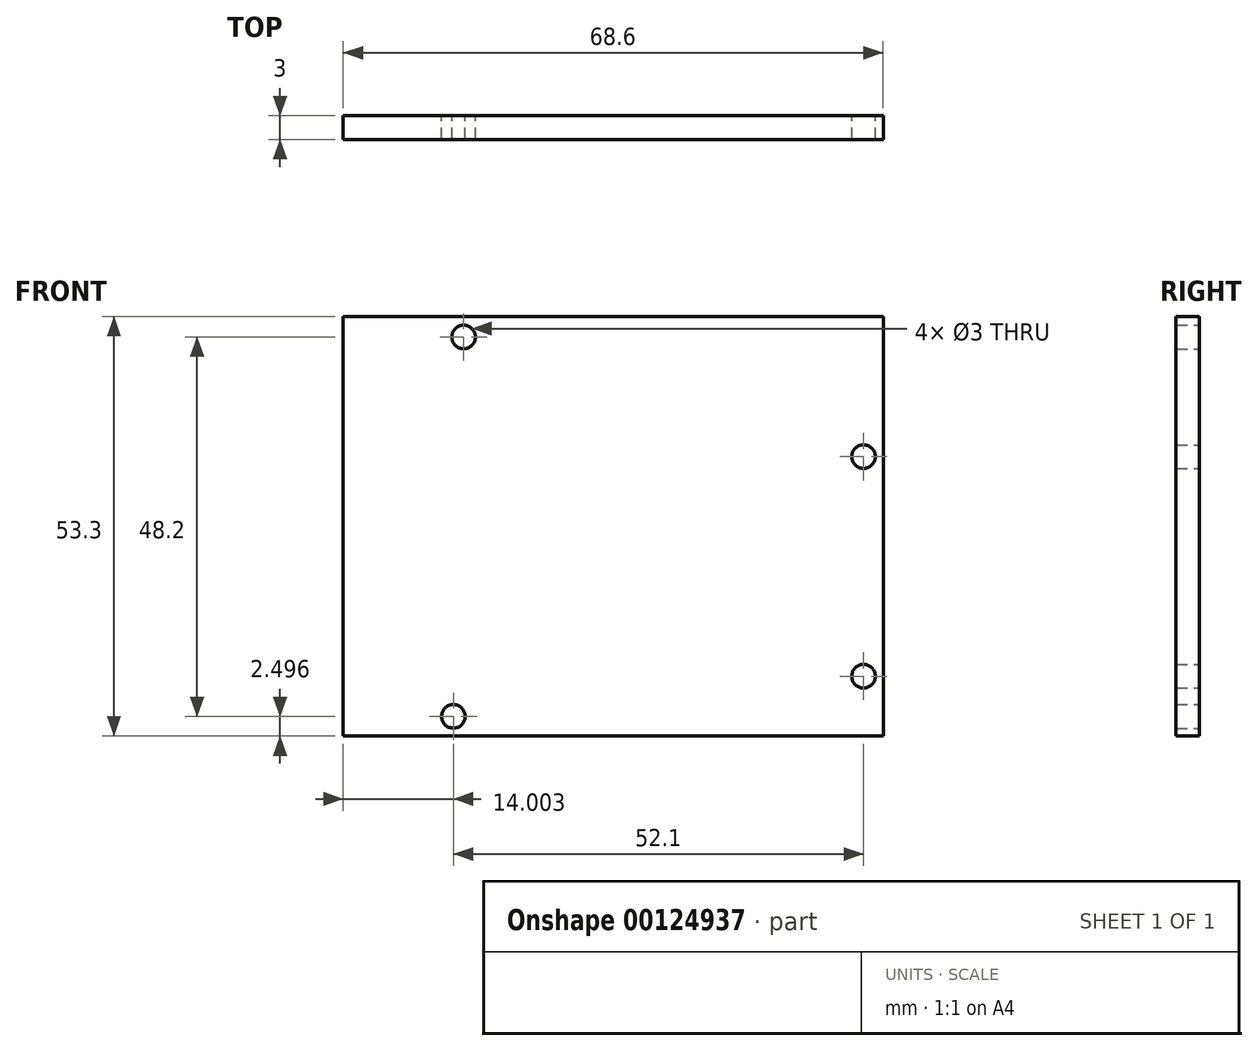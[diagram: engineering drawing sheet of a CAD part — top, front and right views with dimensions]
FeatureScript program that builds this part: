
annotation { "Feature Type Name" : "Feature", "Feature Type Description" : "" }
export const myFeature = defineFeature(function(context is Context, id is Id, definition is map)
    precondition{}
    {
        {
            var Q0;
            Q0=qCreatedBy(makeId("Front.planeOp"),FACE);
            var sketch = newSketch(context, id + "F0", { "sketchPlane" : qUnion([Q0])});
            skLineSegment(sketch, "E0.bottom", {"start": v(-62.54, 81.15) * mm, "end": v(6.06, 81.15) * mm});
            skLineSegment(sketch, "E0.top", {"start": v(-62.54, 27.85) * mm, "end": v(6.06, 27.85) * mm});
            skLineSegment(sketch, "E0.left", {"start": v(-62.54, 81.15) * mm, "end": v(-62.54, 27.85) * mm});
            skLineSegment(sketch, "E0.right", {"start": v(6.06, 81.15) * mm, "end": v(6.06, 27.85) * mm});
            skCircle(sketch, "E1", {"center": v(-48.54, 30.35) * mm, "radius": 1.5 * mm});
            skCircle(sketch, "E2", {"center": v(3.56, 35.45) * mm, "radius": 1.5 * mm});
            skCircle(sketch, "E3", {"center": v(3.56, 63.35) * mm, "radius": 1.5 * mm});
            skCircle(sketch, "E4", {"center": v(-47.24, 78.55) * mm, "radius": 1.5 * mm});
            skSolve(sketch);
        }
        {
            var Q0;
            Q0=makeQuery(id+"F0.imprint","IMPRINT",FACE,{"disambiguationData":[TD([[makeQuery(id+"F0.imprint","IMPRINT",EDGE,{"derivedFrom":sQuery(id+"F0.wireOp",EDGE,"E0.bottom")}),-1.0]])]});
            extrude(context, id + "F1", {"entities" : qUnion([Q0]), "depth" : 3 * mm});
        }
    });
